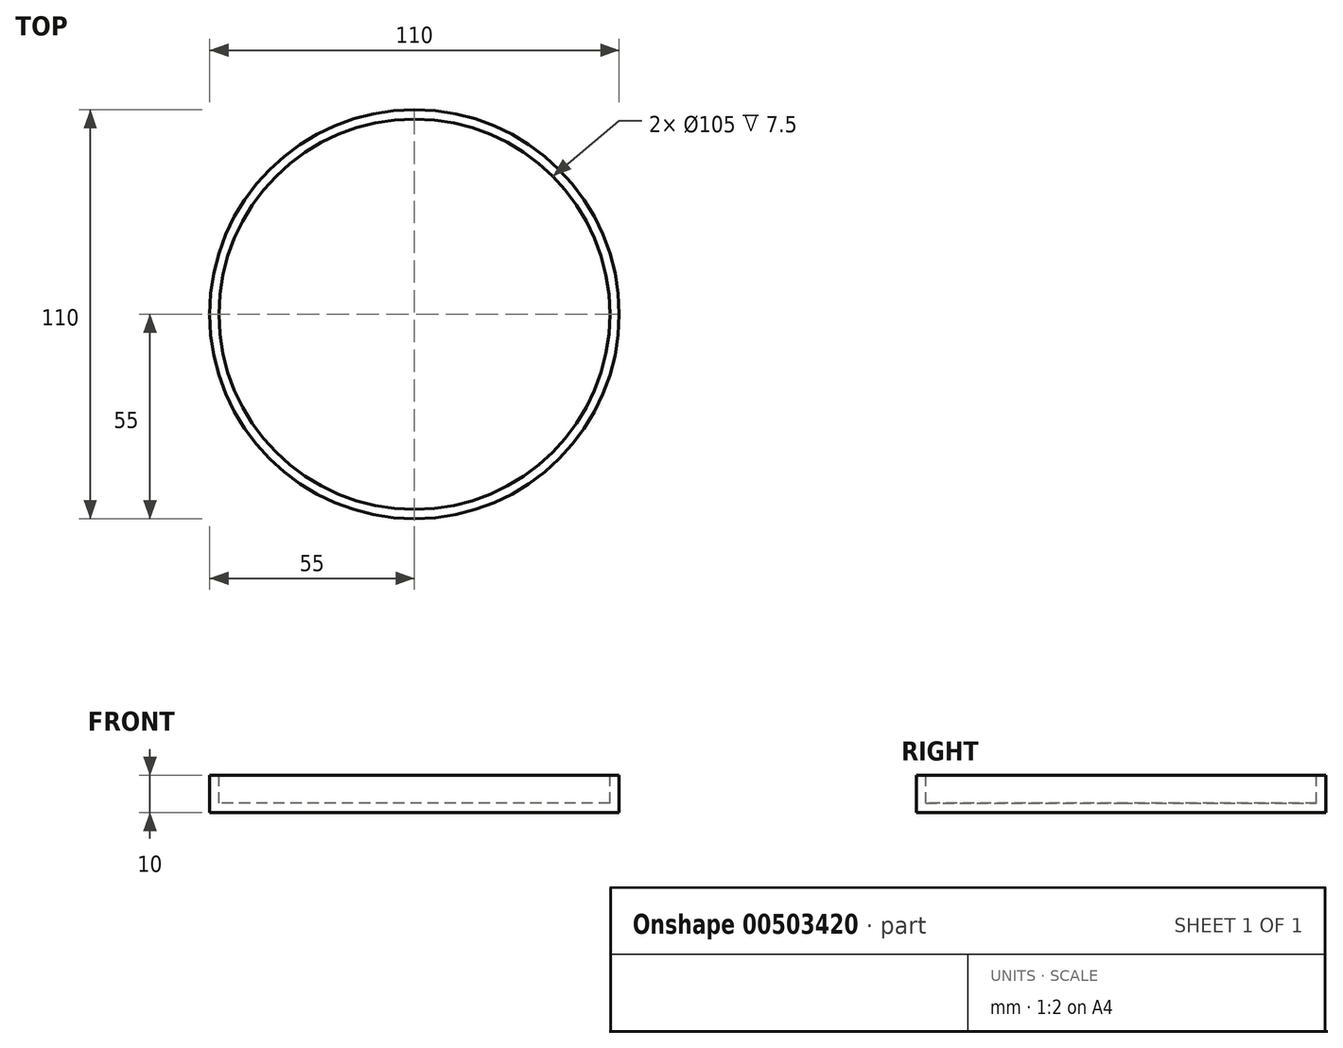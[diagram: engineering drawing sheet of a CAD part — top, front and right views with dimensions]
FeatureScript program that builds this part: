
annotation { "Feature Type Name" : "Feature", "Feature Type Description" : "" }
export const myFeature = defineFeature(function(context is Context, id is Id, definition is map)
    precondition{}
    {
        {
            var Q0;
            Q0=qCreatedBy(makeId("Top.planeOp"),FACE);
            var sketch = newSketch(context, id + "F0", { "sketchPlane" : qUnion([Q0])});
            skCircle(sketch, "E0", {"center": v(0, 0) * mm, "radius": 55 * mm});
            skSolve(sketch);
        }
        {
            var Q0;
            Q0 = qSketchRegion(id + "F0", true);
            extrude(context, id + "F1", {"entities" : qUnion([Q0]), "oppositeDirection" : true, "depth" : 10 * mm});
        }
        {
            var Q0;
            Q0=makeQuery(id+"F1.opExtrude","CAP_FACE",FACE,{"disambiguationData":[OSD([sQuery(id+"F0.wireOp",EDGE,"E0")])],"isStart":true});
            shell(context, id + "F2", {"entities" : qUnion([Q0]), "thickness" : 2.5 * mm});
        }
    });
